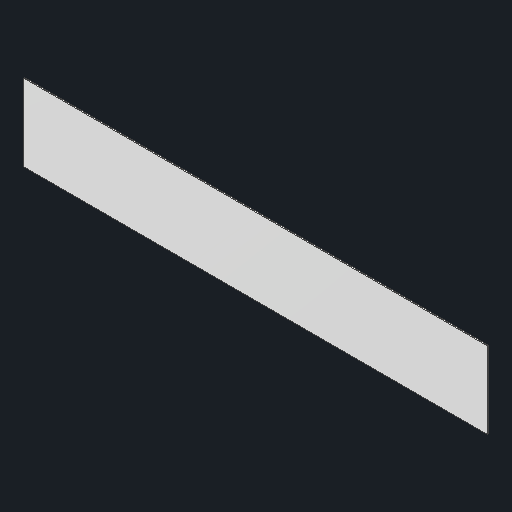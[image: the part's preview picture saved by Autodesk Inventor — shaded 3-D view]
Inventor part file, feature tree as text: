
AUTODESK INVENTOR PART (.ipt)
format: ipt  version: 2024.2 (Build 282272000, 272)  size: 79,872 bytes
history: native  units: in
note: dims shown in document units (in); Inventor stores cm internally (conversion verified against a paired STEP export)
features: extrude x1
ambient origin geometry x8: Origin, YZ Plane, XZ Plane, XY Plane, X Axis, Y Axis, Z Axis, Center Point
bodies: Solid1 (feature_tree)
feature tree (1):
  extrude  "Extrude1"  [1 undecoded]
note: 1 required parameter value undecoded (feature->parameter linkage not recoverable at this tier; creation-order binding heuristic only, values carry confidence <= 0.55)
